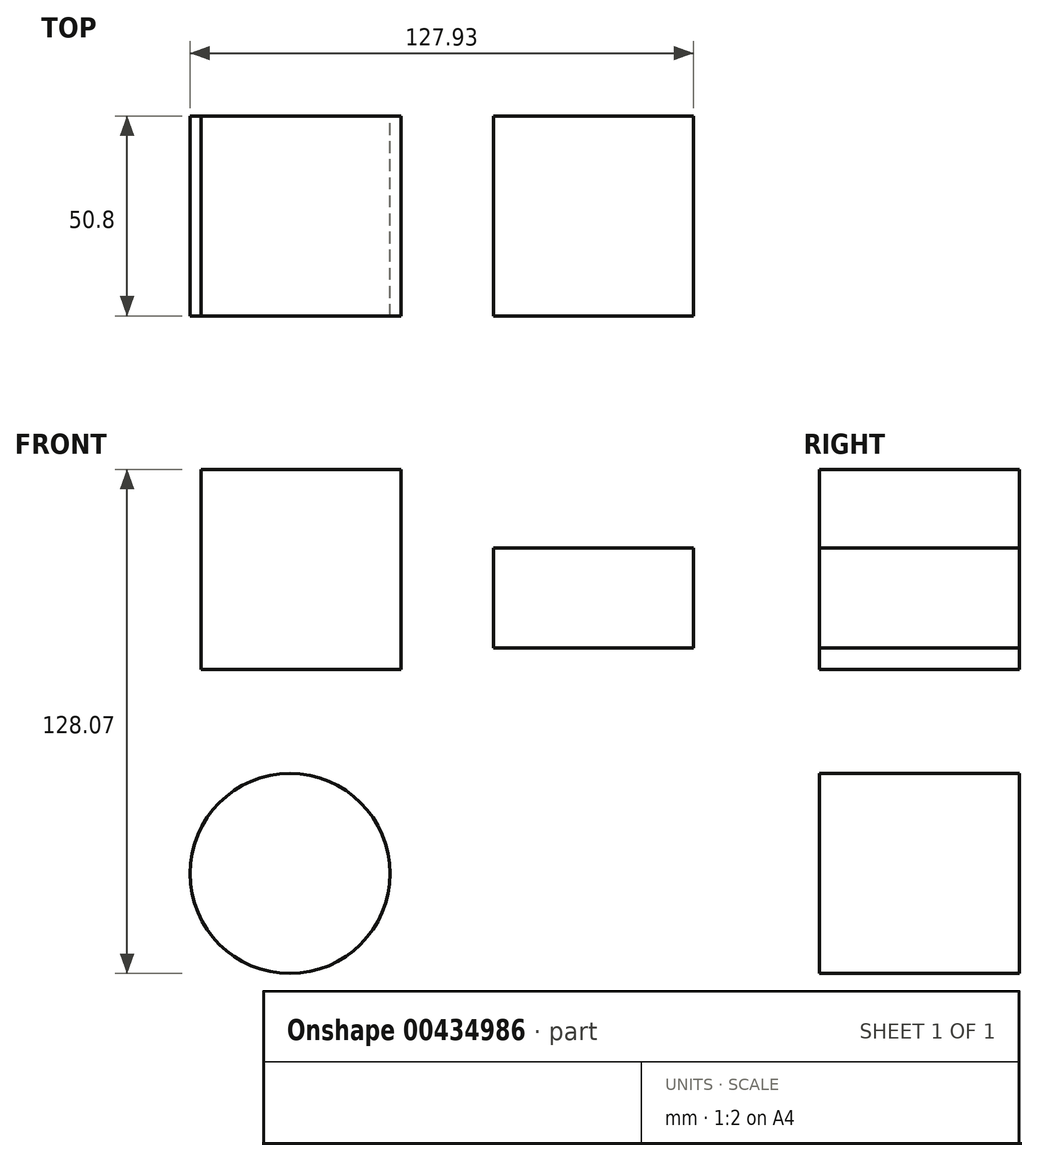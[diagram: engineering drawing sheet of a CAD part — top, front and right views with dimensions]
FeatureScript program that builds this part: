
annotation { "Feature Type Name" : "Feature", "Feature Type Description" : "" }
export const myFeature = defineFeature(function(context is Context, id is Id, definition is map)
    precondition{}
    {
        {
            var Q0;
            Q0=qCreatedBy(makeId("Front.planeOp"),FACE);
            var sketch = newSketch(context, id + "F0", { "sketchPlane" : qUnion([Q0])});
            skLineSegment(sketch, "E0.bottom", {"start": v(-9.44, 74.06) * mm, "end": v(-60.24, 74.06) * mm});
            skLineSegment(sketch, "E0.top", {"start": v(-9.44, 23.26) * mm, "end": v(-60.24, 23.26) * mm});
            skLineSegment(sketch, "E0.left", {"start": v(-9.44, 74.06) * mm, "end": v(-9.44, 23.26) * mm});
            skLineSegment(sketch, "E0.right", {"start": v(-60.24, 74.06) * mm, "end": v(-60.24, 23.26) * mm});
            skPoint(sketch, "E0.middle", {"position": v(-34.84, 48.66) * mm});
            skSolve(sketch);
        }
        {
            var Q0;
            Q0=qCreatedBy(makeId("Front.planeOp"),FACE);
            var sketch = newSketch(context, id + "F1", { "sketchPlane" : qUnion([Q0])});
            skLineSegment(sketch, "E1.bottom", {"start": v(64.85, 28.7) * mm, "end": v(14.05, 28.7) * mm});
            skLineSegment(sketch, "E1.top", {"start": v(64.85, 54.1) * mm, "end": v(14.05, 54.1) * mm});
            skLineSegment(sketch, "E1.left", {"start": v(64.85, 28.7) * mm, "end": v(64.85, 54.1) * mm});
            skLineSegment(sketch, "E1.right", {"start": v(14.05, 28.7) * mm, "end": v(14.05, 54.1) * mm});
            skPoint(sketch, "E1.middle", {"position": v(39.45, 41.4) * mm});
            skSolve(sketch);
        }
        {
            var Q0;
            Q0=qCreatedBy(makeId("Front.planeOp"),FACE);
            var sketch = newSketch(context, id + "F2", { "sketchPlane" : qUnion([Q0])});
            skCircle(sketch, "E2", {"center": v(-37.68, -28.6) * mm, "radius": 25.4 * mm});
            skSolve(sketch);
        }
        {
            var Q0;
            Q0=makeQuery(id+"F0.imprint","IMPRINT",FACE,{"disambiguationData":[TD([[makeQuery(id+"F0.imprint","IMPRINT",EDGE,{"derivedFrom":sQuery(id+"F0.wireOp",EDGE,"E0.bottom")}),1.0]])]});
            extrude(context, id + "F3", {"entities" : qUnion([Q0]), "depth" : 50.8 * mm});
        }
        {
            var Q0;
            Q0=makeQuery(id+"F1.imprint","IMPRINT",FACE,{"disambiguationData":[TD([[makeQuery(id+"F1.imprint","IMPRINT",EDGE,{"derivedFrom":sQuery(id+"F1.wireOp",EDGE,"E1.bottom")}),-1.0]])]});
            extrude(context, id + "F4", {"entities" : qUnion([Q0]), "depth" : 50.8 * mm});
        }
        {
            var Q0;
            Q0=makeQuery(id+"F2.imprint","IMPRINT",FACE,{"disambiguationData":[TD([[makeQuery(id+"F2.imprint","IMPRINT",EDGE,{"derivedFrom":sQuery(id+"F2.wireOp",EDGE,"E2")}),1.0]])]});
            extrude(context, id + "F5", {"entities" : qUnion([Q0]), "depth" : 50.8 * mm});
        }
    });
